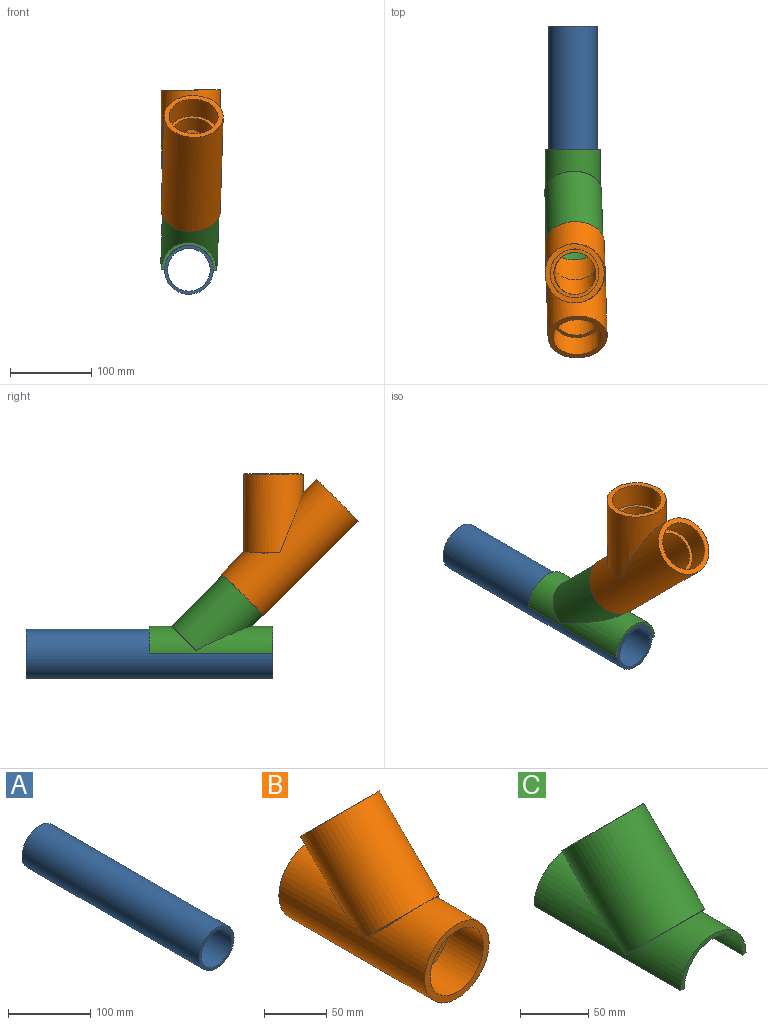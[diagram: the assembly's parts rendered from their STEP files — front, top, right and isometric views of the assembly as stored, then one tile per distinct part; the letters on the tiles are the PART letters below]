
ASSEMBLY  parts=3 mates=3
PART A: 4 faces, bbox 60.3x304.8x60.3 mm
  f0: cylinder r=26.25mm len=304.8mm, axis (0,1,0), area 50273.5mm2, adj f2,f3
  f1: cylinder r=30.16mm len=304.8mm, axis (0,1,0), area 57764.7mm2, adj f2,f3
  f2: plane 60.33x60.33mm, normal (0,-1,0), area 693.2mm2, adj f0,f1
  f3: plane 60.33x60.33mm, normal (0,1,0), area 693.2mm2, adj f0,f1
PART B: 17 faces, bbox 73x165.1x140.9 mm
  f0: cylinder r=26mm len=96.9mm, axis (0,-1,0), area 12005mm2, adj f3,f4,f8
  f1: plane 73.03x73.03mm, normal (0,1,0), area 1330.1mm2, adj f2,f7
  f2: cylinder r=30.16mm len=60.33mm, axis (0,-1,0), area 5559.8mm2, adj f1,f3,f16
  f3: plane 60.33x60.33mm, normal (0,1,0), area 734.9mm2, adj f0,f2,f16
  f4: plane 60.33x60.33mm, normal (0,-1,0), area 734.9mm2, adj f0,f5
  f5: cylinder r=30.16mm len=60.33mm, axis (0,-1,0), area 7365mm2, adj f4,f6
  f6: plane 73.03x73.03mm, normal (0,-1,0), area 1330.1mm2, adj f5,f7
  f7: cylinder r=36.51mm len=165.1mm, axis (0,-1,0), area 31004.5mm2, adj f1,f6,f9,f10,f14
  f8: cylinder r=26mm len=94.6mm, axis (0,-0.71,-0.71), area 9536.4mm2, adj f0,f13
  f9: cone r=26mm half-angle=67.5deg, axis (0,0.71,0.71), area 104.8mm2, adj f7,f10
  f10: cylinder r=36.51mm len=119.52mm, axis (0,-0.71,-0.71), area 17226.8mm2, adj f7,f9,f11,f14
  f11: plane 73.03x51.64mm, normal (0,0.71,0.71), area 1330.1mm2, adj f10,f12
  f12: cylinder r=30.16mm len=63.4mm, axis (0,-0.71,-0.71), area 5559.8mm2, adj f11,f13,f15
  f13: plane 60.33x42.66mm, normal (0,0.71,0.71), area 734.9mm2, adj f8,f12,f15
  f14: cone r=26mm half-angle=67.5deg, axis (0,0.71,0.71), area 104.8mm2, adj f7,f10
  f15: cylinder r=36.51mm len=1.1mm, axis (0,-1,0), area 0mm2, adj f12,f13
  f16: cylinder r=36.51mm len=1.11mm, axis (0,-0.71,-0.71), area 0mm2, adj f2,f3
PART C: 13 faces, bbox 69.9x152.4x112.8 mm
  f0: cylinder r=33.97mm len=152.4mm, axis (0,1,0), area 10034.6mm2, adj f1,f2,f3,f4,f6,f7,f8
  f1: plane 152.4x3.81mm, normal (0,0,-1), area 580.6mm2, adj f0,f3,f4,f12
  f2: plane 152.4x3.81mm, normal (0,0,-1), area 580.6mm2, adj f0,f3,f4,f12
  f3: plane 67.95x33.97mm, normal (0,-1,0), area 383.8mm2, adj f0,f1,f2,f12
  f4: plane 67.95x33.97mm, normal (0,1,0), area 383.8mm2, adj f0,f1,f2,f12
  f5: cylinder r=26.25mm len=85.7mm, axis (0,-0.71,-0.71), area 8378.7mm2, adj f11,f12
  f6: cylinder r=34.92mm len=112.84mm, axis (0,-0.71,-0.71), area 15401.6mm2, adj f0,f7,f8,f10
  f7: plane 34.93x30.84mm, normal (0,-0.71,-0.71), area 126.7mm2, adj f0,f6
  f8: plane 34.93x30.84mm, normal (0,-0.71,-0.71), area 126.7mm2, adj f0,f6
  f9: cylinder r=30.16mm len=60.33mm, axis (0,-0.71,-0.71), area 3656.3mm2, adj f10,f11
  f10: plane 69.85x49.39mm, normal (0,0.71,0.71), area 973.8mm2, adj f6,f9
  f11: plane 60.33x42.66mm, normal (0,0.71,0.71), area 693.2mm2, adj f5,f9
  f12: cylinder r=30.16mm len=152.4mm, axis (0,1,0), area 10941.5mm2, adj f1,f2,f3,f4,f5
PLACE A t=(-26.25,0,0)mm
PLACE B rot(axis=(0.01,-0.38,-0.92),178deg) t=(-22.84,-153.12,110.84)mm
PLACE C rot(axis=(0.02,0,1),180deg) t=(-26.25,-76.2,0)mm
MATE cylindrical C.f5 <-> B.f0  axis (-0.02,0.71,-0.71) through (-24.99,-83.23,40.98)mm
MATE planar C.f5 <-> B.f0  axis (0.02,-0.71,0.71) through (-24.01,-114.95,72.69)mm
MATE revolute A.f1 <-> C.f12  axis (0,1,0) through (-26.25,0,0)mm
